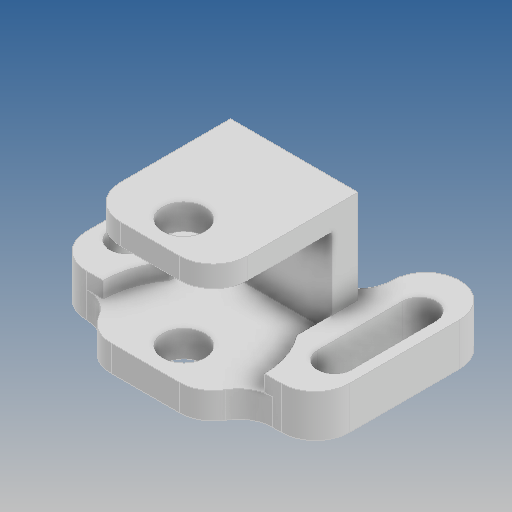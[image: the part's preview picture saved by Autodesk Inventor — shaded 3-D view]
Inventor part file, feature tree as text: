
AUTODESK INVENTOR PART (.ipt)
format: ipt  version: 2020 (Build 240168000, 168)  size: 283,648 bytes
history: native  units: mm
features: extrude x9, sketch x9, other x2, fillet x1, reference x1
ambient origin geometry x8: Origin, YZ Plane, XZ Plane, XY Plane, X Axis, Y Axis, Z Axis, Center Point
bodies: Solid1 (feature_tree)
feature tree (22):
  extrude  "Extrusion1"  Depth=15.0mm
  extrude  "Extrusion2"  Depth=8.0mm
  extrude  "Extrusion3"  Depth=3.1mm
  extrude  "Extrusion4"  Depth=2.5mm
  extrude  "Extrusion5"  Depth=5.0mm
  extrude  "Extrusion6"  TaperAngle=0.0deg  [1 undecoded]
  extrude  "Extrusion7"  Depth=0.5mm TaperAngle=0.0deg
  fillet  "Fillet1"  Radius=7.0mm
  extrude  "Extrusion8"  Depth=4.0mm
  extrude  "Extrusion9"  TaperAngle=0.0deg  [1 undecoded]
  sketch  "Sketch1"  dims[d0=16.0mm d1=15.0mm]
  sketch  "Sketch2"  dims[d2=5.0mm d3=8.0mm]
  sketch  "Sketch3"  dims[d4=17.0mm d5=0.0mm d6=3.1mm]
  sketch  "Sketch4"  dims[d7=10.4mm d8=2.5mm]
  sketch  "Sketch5"  dims[d9=14.0mm d10=0.0mm d11=5.0mm]
  sketch  "Sketch6"  dims[d12=4.0mm d13=0.0mm d14=0.0mm]
  sketch  "Sketch8"  dims[d15=7.0mm d16=0.5mm d17=0.0mm d18=7.0mm]
  sketch  "Sketch9"  dims[d19=0.5mm d20=0.0mm d21=4.0mm]
  sketch  "Sketch10"  dims[d22=4.0mm d23=0.0mm d24=0.0mm d25=8.0mm d26=0.5mm d27=0.0mm d28=4.0mm d30=4.0mm d31=10.0mm d32=0.0mm d33=0.0mm d34=19.0mm d35=14.0mm d36=0.0mm]
  reference  "Reference1"
  other  "30-00 Injectomat suplimentar.iam"
  other  "0008-30-1012 16T W6 B3 Without T_Shrinkwrap_1:1"
note: 2 required parameter values undecoded (feature->parameter linkage not recoverable at this tier; creation-order binding heuristic only, values carry confidence <= 0.55)
